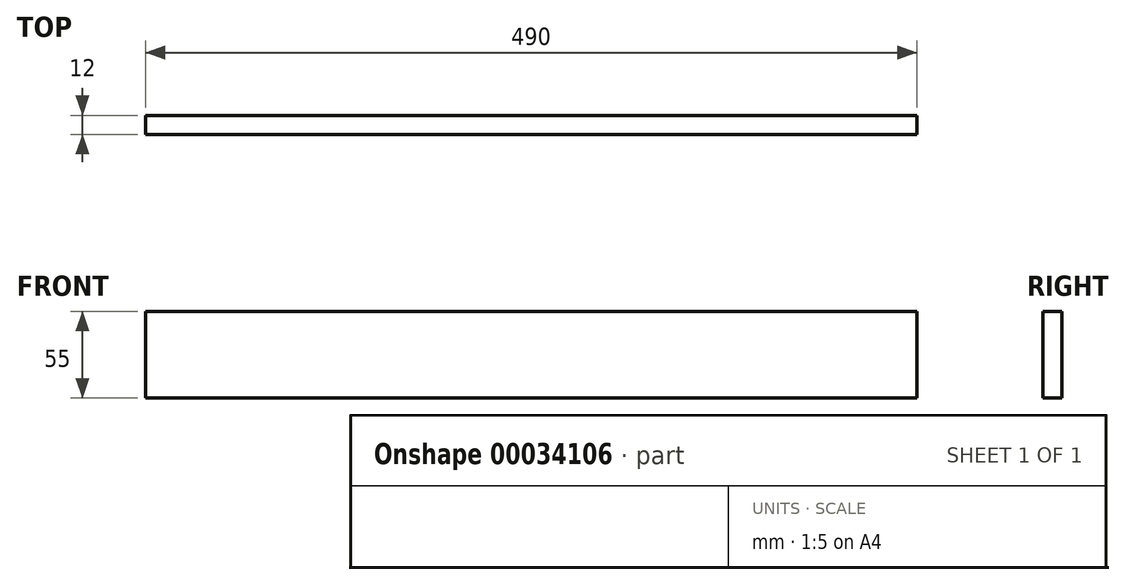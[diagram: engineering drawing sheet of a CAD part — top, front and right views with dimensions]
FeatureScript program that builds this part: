
annotation { "Feature Type Name" : "Feature", "Feature Type Description" : "" }
export const myFeature = defineFeature(function(context is Context, id is Id, definition is map)
    precondition{}
    {
        {
            var Q0;
            Q0=qCreatedBy(makeId("Front.planeOp"),FACE);
            var sketch = newSketch(context, id + "F0", { "sketchPlane" : qUnion([Q0])});
            skLineSegment(sketch, "E0.rect.bottom", {"start": v(245, -27.5) * mm, "end": v(-245, -27.5) * mm});
            skLineSegment(sketch, "E0.rect.top", {"start": v(245, 27.5) * mm, "end": v(-245, 27.5) * mm});
            skLineSegment(sketch, "E0.rect.left", {"start": v(245, -27.5) * mm, "end": v(245, 27.5) * mm});
            skLineSegment(sketch, "E0.rect.right", {"start": v(-245, -27.5) * mm, "end": v(-245, 27.5) * mm});
            skPoint(sketch, "E0.rect.middle", {"position": v(0, 0) * mm});
            skSolve(sketch);
        }
        {
            var Q0;
            Q0=makeQuery(id+"F0.imprint","IMPRINT",FACE,{"disambiguationData":[TD([[makeQuery(id+"F0.imprint","IMPRINT",EDGE,{"derivedFrom":sQuery(id+"F0.wireOp",EDGE,"E0.rect.bottom")}),-1.0]])]});
            extrude(context, id + "F1", {"entities" : qUnion([Q0]), "depth" : 12 * mm});
        }
    });
